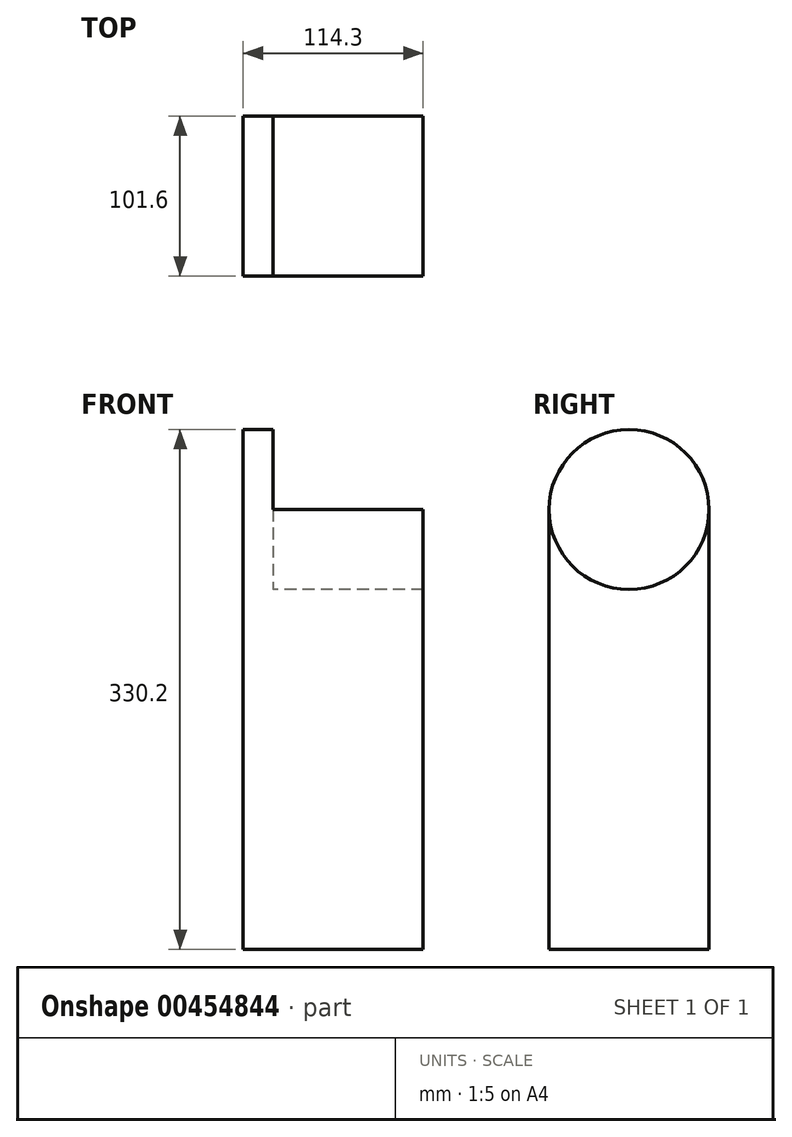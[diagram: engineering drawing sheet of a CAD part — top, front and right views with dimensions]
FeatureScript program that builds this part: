
annotation { "Feature Type Name" : "Feature", "Feature Type Description" : "" }
export const myFeature = defineFeature(function(context is Context, id is Id, definition is map)
    precondition{}
    {
        {
            var Q0;
            Q0=qCreatedBy(makeId("Right.planeOp"),FACE);
            var sketch = newSketch(context, id + "F0", { "sketchPlane" : qUnion([Q0])});
            skCircle(sketch, "E0", {"center": v(0, 0) * mm, "radius": 50.8 * mm});
            skLineSegment(sketch, "E1.bottom", {"start": v(50.8, 0) * mm, "end": v(-50.8, 0) * mm});
            skLineSegment(sketch, "E1.top", {"start": v(50.8, -101.6) * mm, "end": v(-50.8, -101.6) * mm});
            skLineSegment(sketch, "E1.left", {"start": v(50.8, 0) * mm, "end": v(50.8, -101.6) * mm});
            skLineSegment(sketch, "E1.right", {"start": v(-50.8, 0) * mm, "end": v(-50.8, -101.6) * mm});
            skPoint(sketch, "E1.middle", {"position": v(0, -50.8) * mm});
            skSolve(sketch);
        }
        {
            var Q0;
            Q0=qSketchRegion(id+"F0",true);
            extrude(context, id + "F1", {"entities" : qUnion([Q0]), "depth" : 19.05 * mm, "offsetDistance" : 25.4 * mm});
        }
        {
            var Q0;
            Q0=makeQuery(id+"F0.imprint","IMPRINT",FACE,{"disambiguationData":[TD([[makeQuery(id+"F0.imprint","IMPRINT",EDGE,{"derivedFrom":sQuery(id+"F0.wireOp",EDGE,"E1.top")}),-1.0]])]});
            extrude(context, id + "F2", {"entities" : qUnion([Q0]), "operationType" : NewBodyOperationType.ADD, "depth" : 114.3 * mm, "offsetDistance" : 25.4 * mm});
        }
        {
            var Q0;
            {var subQ0=sQuery(id+"F0.wireOp",EDGE,"E1.top");Q0=makeQuery(id+"F2.boolean.opBoolean","MERGE",FACE,{"derivedFrom":[makeQuery(id+"F1.opExtrude","SWEPT_FACE",FACE,{"disambiguationData":[OSD([subQ0])]}),makeQuery(id+"F2.opExtrude","SWEPT_FACE",FACE,{"disambiguationData":[OSD([subQ0])]})]});}
            var sketch = newSketch(context, id + "F3", { "sketchPlane" : qUnion([Q0])});
            skLineSegment(sketch, "E2.bottom", {"start": v(0, 50.8) * mm, "end": v(114.3, 50.8) * mm});
            skLineSegment(sketch, "E2.top", {"start": v(0, -50.8) * mm, "end": v(114.3, -50.8) * mm});
            skLineSegment(sketch, "E2.left", {"start": v(0, 50.8) * mm, "end": v(0, -50.8) * mm});
            skLineSegment(sketch, "E2.right", {"start": v(114.3, 50.8) * mm, "end": v(114.3, -50.8) * mm});
            skSolve(sketch);
        }
        {
            var Q0;
            Q0=qSketchRegion(id+"F3",true);
            extrude(context, id + "F4", {"entities" : qUnion([Q0]), "operationType" : NewBodyOperationType.ADD, "depth" : 177.8 * mm, "offsetDistance" : 25.4 * mm});
        }
    });
